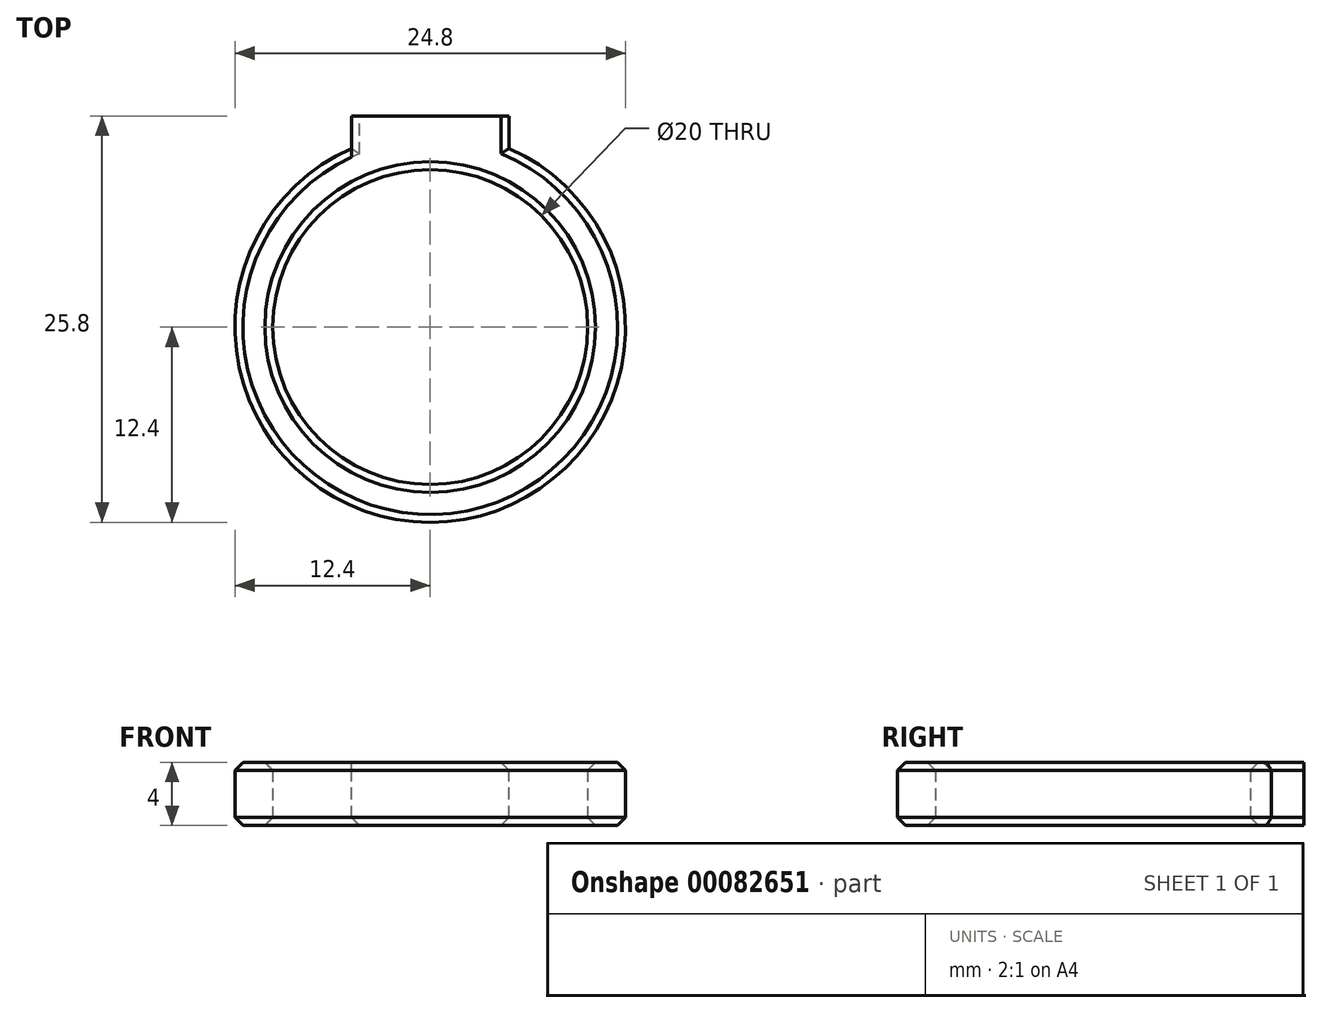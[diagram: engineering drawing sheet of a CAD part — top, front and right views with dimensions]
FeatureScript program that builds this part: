
annotation { "Feature Type Name" : "Feature", "Feature Type Description" : "" }
export const myFeature = defineFeature(function(context is Context, id is Id, definition is map)
    precondition{}
    {
        {
            var Q0;
            Q0=qCreatedBy(makeId("Front.planeOp"),FACE);
            var sketch = newSketch(context, id + "F0", { "sketchPlane" : qUnion([Q0])});
            skLineSegment(sketch, "E0.bottom", {"start": v(10, 0) * mm, "end": v(12.4, 0) * mm});
            skLineSegment(sketch, "E0.top", {"start": v(10, 4) * mm, "end": v(12.4, 4) * mm});
            skLineSegment(sketch, "E0.left", {"start": v(10, 0) * mm, "end": v(10, 4) * mm});
            skLineSegment(sketch, "E0.right", {"start": v(12.4, 0) * mm, "end": v(12.4, 4) * mm});
            skLineSegment(sketch, "E1", {"start": v(0, 0) * mm, "end": v(0, 10.45) * mm, "construction": true});
            skSolve(sketch);
        }
        {
            var Q0;
            Q0=makeQuery(id+"F0.imprint","IMPRINT",FACE,{"disambiguationData":[TD([[makeQuery(id+"F0.imprint","IMPRINT",EDGE,{"derivedFrom":sQuery(id+"F0.wireOp",EDGE,"E0.bottom")}),1.0]])]});
            var Q1;
            Q1=sQuery(id+"F0.wireOp",EDGE,"E1");
            revolve(context, id + "F1", {"entities" : qUnion([Q0]), "axis" : qUnion([Q1]), "revolveType" : RevolveType.FULL});
        }
        {
            var Q0;
            Q0=makeQuery(id+"F1.opRevolve","SWEPT_FACE",FACE,{"disambiguationData":[OSD([sQuery(id+"F0.wireOp",EDGE,"E0.top")])]});
            var sketch = newSketch(context, id + "F2", { "sketchPlane" : qUnion([Q0])});
            skLineSegment(sketch, "E2.bottom", {"start": v(-5, 11.35) * mm, "end": v(5, 11.35) * mm});
            skLineSegment(sketch, "E2.top", {"start": v(-5, 13.4) * mm, "end": v(5, 13.4) * mm});
            skLineSegment(sketch, "E2.left", {"start": v(-5, 11.35) * mm, "end": v(-5, 13.4) * mm});
            skLineSegment(sketch, "E2.right", {"start": v(5, 11.35) * mm, "end": v(5, 13.4) * mm});
            skSolve(sketch);
        }
        {
            var Q0;
            Q0 = qSketchRegion(id + "F2", true);
            var Q1;
            Q1=makeQuery(id+"F1.opRevolve","SWEPT_FACE",FACE,{"disambiguationData":[OSD([sQuery(id+"F0.wireOp",EDGE,"E0.bottom")])]});
            extrude(context, id + "F3", {"entities" : qUnion([Q0]), "operationType" : NewBodyOperationType.ADD, "endBound" : BoundingType.UP_TO_SURFACE, "oppositeDirection" : true, "endBoundEntityFace" : qUnion([Q1]), "depth" : 25 * mm});
        }
        {
            var Q0;
            Q0=makeQuery(id+"F1.opRevolve","SWEPT_EDGE",EDGE,{"disambiguationData":[OSD([sQuery(id+"F0.wireOp",EDGE,"E0.top"),sQuery(id+"F0.wireOp",EDGE,"E0.right")])]});
            var Q1;
            Q1=makeQuery(id+"F3.opExtrude","CAP_EDGE",EDGE,{"disambiguationData":[OSD([sQuery(id+"F2.wireOp",EDGE,"E2.right")])],"isStart":true});
            var Q2;
            Q2=makeQuery(id+"F1.opRevolve","SWEPT_EDGE",EDGE,{"disambiguationData":[OSD([sQuery(id+"F0.wireOp",EDGE,"E0.bottom"),sQuery(id+"F0.wireOp",EDGE,"E0.right")])]});
            var Q3;
            Q3=makeQuery(id+"F3.opExtrude","CAP_EDGE",EDGE,{"disambiguationData":[OSD([sQuery(id+"F2.wireOp",EDGE,"E2.right")])],"isStart":false});
            var Q4;
            Q4=makeQuery(id+"F3.opExtrude","CAP_EDGE",EDGE,{"disambiguationData":[OSD([sQuery(id+"F2.wireOp",EDGE,"E2.left")])],"isStart":false});
            var Q5;
            Q5=makeQuery(id+"F1.opRevolve","SWEPT_EDGE",EDGE,{"disambiguationData":[OSD([sQuery(id+"F0.wireOp",EDGE,"E0.top"),sQuery(id+"F0.wireOp",EDGE,"E0.left")])]});
            var Q6;
            Q6=makeQuery(id+"F1.opRevolve","SWEPT_EDGE",EDGE,{"disambiguationData":[OSD([sQuery(id+"F0.wireOp",EDGE,"E0.bottom"),sQuery(id+"F0.wireOp",EDGE,"E0.left")])]});
            chamfer(context, id + "F4", {"entities" : qUnion([Q0, Q1, Q2, Q3, Q4, Q5, Q6]), "width" : 0.5 * mm, "tangentPropagation" : true});
        }
    });
